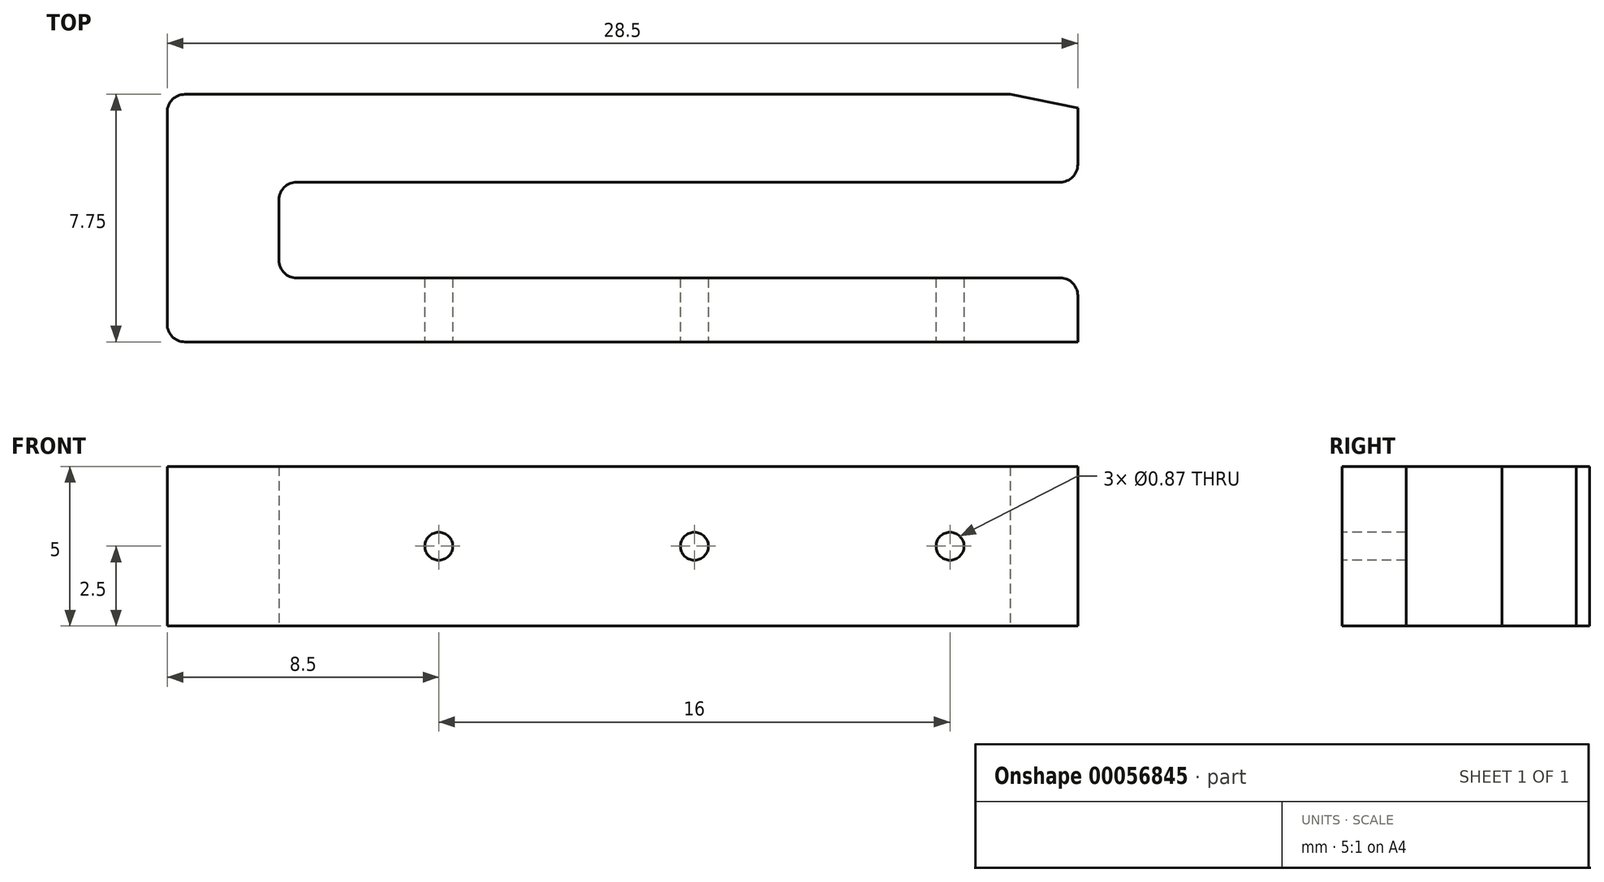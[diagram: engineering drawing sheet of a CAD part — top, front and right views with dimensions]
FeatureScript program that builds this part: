
annotation { "Feature Type Name" : "Feature", "Feature Type Description" : "" }
export const myFeature = defineFeature(function(context is Context, id is Id, definition is map)
    precondition{}
    {
        {
            var Q0;
            Q0=qCreatedBy(makeId("Top.planeOp"),FACE);
            var sketch = newSketch(context, id + "F0", { "sketchPlane" : qUnion([Q0])});
            skLineSegment(sketch, "E0", {"start": v(-11.4, 0) * mm, "end": v(12.89, 0) * mm, "construction": true});
            skLineSegment(sketch, "E1.0", {"start": v(-11.4, 7.75) * mm, "end": v(12.89, 7.75) * mm});
            skLineSegment(sketch, "E2.0", {"start": v(-9.45, 2) * mm, "end": v(12.89, 2) * mm});
            skLineSegment(sketch, "E3.0", {"start": v(-11.4, -5) * mm, "end": v(12.89, -5) * mm});
            skLineSegment(sketch, "E4.0", {"start": v(-11.4, 5) * mm, "end": v(12.89, 5) * mm, "construction": true});
            skLineSegment(sketch, "E5", {"start": v(0, 8.04) * mm, "end": v(0, -1.19) * mm, "construction": true});
            skLineSegment(sketch, "E6.0", {"start": v(-10, 8.04) * mm, "end": v(-10, 7.75) * mm, "construction": true});
            skLineSegment(sketch, "E7.0", {"start": v(15, 8.04) * mm, "end": v(15, -1.19) * mm, "construction": true});
            skLineSegment(sketch, "E8.0", {"start": v(-13.5, 8.04) * mm, "end": v(-13.5, -1.19) * mm, "construction": true});
            skLineSegment(sketch, "E9", {"start": v(-10, 4.45) * mm, "end": v(-10, 2.55) * mm});
            skLineSegment(sketch, "E10.trimOffspring", {"start": v(-10, 5) * mm, "end": v(-10, -1.19) * mm, "construction": true});
            skLineSegment(sketch, "E11", {"start": v(-9.45, 5) * mm, "end": v(14.45, 5) * mm});
            skLineSegment(sketch, "E12", {"start": v(15, 5.55) * mm, "end": v(15, 7.33) * mm});
            skLineSegment(sketch, "E13", {"start": v(15, 7.33) * mm, "end": v(12.89, 7.75) * mm});
            skLineSegment(sketch, "E14", {"start": v(-11.4, 7.75) * mm, "end": v(-12.95, 7.75) * mm});
            skLineSegment(sketch, "E15", {"start": v(-13.5, 7.2) * mm, "end": v(-13.5, 0.55) * mm});
            skLineSegment(sketch, "E16", {"start": v(-12.95, 0) * mm, "end": v(15, 0) * mm});
            skLineSegment(sketch, "E17", {"start": v(15, 0) * mm, "end": v(15, 1.45) * mm});
            skLineSegment(sketch, "E18", {"start": v(14.45, 2) * mm, "end": v(12.89, 2) * mm});
            skPoint(sketch, "E19.visualSharp", {"position": v(15, 5) * mm});
            skArc(sketch, "E19.filletArc", {"start": v(14.45, 5) * mm, "mid": v(14.84, 5.16) * mm, "end": v(15, 5.55) * mm});
            skPoint(sketch, "E20.visualSharp", {"position": v(15, 2) * mm});
            skArc(sketch, "E20.filletArc", {"start": v(15, 1.45) * mm, "mid": v(14.84, 1.84) * mm, "end": v(14.45, 2) * mm});
            skPoint(sketch, "E21.visualSharp", {"position": v(-10, 5) * mm});
            skArc(sketch, "E21.filletArc", {"start": v(-9.45, 5) * mm, "mid": v(-9.84, 4.84) * mm, "end": v(-10, 4.45) * mm});
            skArc(sketch, "E22.filletArc", {"start": v(-10, 2.55) * mm, "mid": v(-9.84, 2.16) * mm, "end": v(-9.45, 2) * mm});
            skPoint(sketch, "E23.visualSharp", {"position": v(-13.5, 7.75) * mm});
            skArc(sketch, "E23.filletArc", {"start": v(-12.95, 7.75) * mm, "mid": v(-13.34, 7.59) * mm, "end": v(-13.5, 7.2) * mm});
            skPoint(sketch, "E24.visualSharp", {"position": v(-13.5, 0) * mm});
            skArc(sketch, "E24.filletArc", {"start": v(-13.5, 0.55) * mm, "mid": v(-13.34, 0.16) * mm, "end": v(-12.95, 0) * mm});
            skSolve(sketch);
        }
        {
            var Q0;
            Q0=makeQuery(id+"F0.imprint","IMPRINT",FACE,{"disambiguationData":[TD([[makeQuery(id+"F0.imprint","IMPRINT",EDGE,{"derivedFrom":sQuery(id+"F0.wireOp",EDGE,"E1.0")}),-1.0]])]});
            extrude(context, id + "F1", {"entities" : qUnion([Q0]), "depth" : 5 * mm});
        }
        {
            var Q0;
            Q0=makeQuery(id+"F1.opExtrude","SWEPT_FACE",FACE,{"disambiguationData":[OSD([sQuery(id+"F0.wireOp",EDGE,"E16")])]});
            var sketch = newSketch(context, id + "F2", { "sketchPlane" : qUnion([Q0])});
            skLineSegment(sketch, "E25.0.0", {"start": v(-12.95, 0) * mm, "end": v(15, 0) * mm});
            skLineSegment(sketch, "E25.0.1", {"start": v(15, 0) * mm, "end": v(15, 5) * mm});
            skLineSegment(sketch, "E25.0.2", {"start": v(15, 5) * mm, "end": v(-12.95, 5) * mm});
            skLineSegment(sketch, "E25.0.3", {"start": v(-12.95, 5) * mm, "end": v(-12.95, 0) * mm});
            skLineSegment(sketch, "E26.0.1", {"start": v(-10, 0) * mm, "end": v(-10, 5) * mm});
            skLineSegment(sketch, "E26.0.3", {"start": v(-10, 5) * mm, "end": v(-10, 0) * mm});
            skLineSegment(sketch, "E27.0", {"start": v(-5, 5) * mm, "end": v(-5, 0) * mm, "construction": true});
            skCircle(sketch, "E28", {"center": v(-5, 2.5) * mm, "radius": 0.44 * mm});
            skCircle(sketch, "E29.1.0.0", {"center": v(3, 2.5) * mm, "radius": 0.44 * mm});
            skCircle(sketch, "E29.2.0.0", {"center": v(11, 2.5) * mm, "radius": 0.44 * mm});
            skLineSegment(sketch, "E29.direction1", {"start": v(-5, 2.5) * mm, "end": v(3, 2.5) * mm, "construction": true});
            skSolve(sketch);
        }
        {
            var Q0;
            Q0=makeQuery(id+"F2.imprint","IMPRINT",FACE,{"disambiguationData":[TD([[makeQuery(id+"F2.imprint","IMPRINT",EDGE,{"derivedFrom":sQuery(id+"F2.wireOp",EDGE,"E29.2.0.0")}),1.0]])]});
            var Q1;
            Q1=makeQuery(id+"F2.imprint","IMPRINT",FACE,{"disambiguationData":[TD([[makeQuery(id+"F2.imprint","IMPRINT",EDGE,{"derivedFrom":sQuery(id+"F2.wireOp",EDGE,"E29.1.0.0")}),1.0]])]});
            var Q2;
            Q2=makeQuery(id+"F2.imprint","IMPRINT",FACE,{"disambiguationData":[TD([[makeQuery(id+"F2.imprint","IMPRINT",EDGE,{"derivedFrom":sQuery(id+"F2.wireOp",EDGE,"E28")}),1.0]])]});
            extrude(context, id + "F3", {"entities" : qUnion([Q0, Q1, Q2]), "operationType" : NewBodyOperationType.REMOVE, "oppositeDirection" : true, "depth" : 4 * mm});
        }
    });
